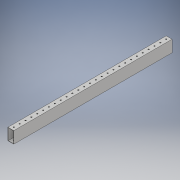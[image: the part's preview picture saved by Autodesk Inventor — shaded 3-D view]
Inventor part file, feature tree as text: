
AUTODESK INVENTOR PART (.ipt)
format: ipt  version: 2018 (Build 220112000, 112)  size: 206,336 bytes
history: native  units: in
note: dims shown in document units (in); Inventor stores cm internally (conversion verified against a paired STEP export)
features: extrude x2, sketch x2
ambient origin geometry x8: Origin, YZ Plane, XZ Plane, XY Plane, X Axis, Y Axis, Z Axis, Center Point
bodies: Solid1 (feature_tree)
feature tree (4):
  extrude  "Extrusion1"  Depth=2.0in
  extrude  "Extrusion2"  Depth=27.0in TaperAngle=0.0deg
  sketch  "Sketch1"  dims[d0=1.0in d1=2.0in]
  sketch  "Sketch2"  dims[d2=0.0625in d3=27.0in d4=0.0in d5=0.5in d6=1.0in d7=1.0in d8=1.0in d9=1.0in d10=1.0in d11=1.0in d12=1.0in d13=1.0in d14=1.0in d15=1.0in d16=1.0in d17=1.0in d18=1.0in d19=1.0in d20=1.0in d21=1.0in d22=1.0in d23=1.0in d24=1.0in d25=1.0in d26=1.0in d27=1.0in d28=1.0in d29=1.0in d30=1.0in d31=1.0in d32=1.0in d33=1.0in d34=0.203in d35=0.203in d36=0.203in d37=0.203in d38=0.203in d39=0.203in d40=0.203in d41=0.203in d42=0.203in d43=0.203in d44=0.203in d45=0.203in d46=0.203in d47=0.203in d48=0.203in d49=0.203in d50=0.203in d51=0.203in d52=0.203in d53=0.203in d54=0.203in d55=0.203in d56=0.203in d57=0.203in d58=0.203in d59=0.203in d60=0.203in d61=27.0in d62=0.0in]
